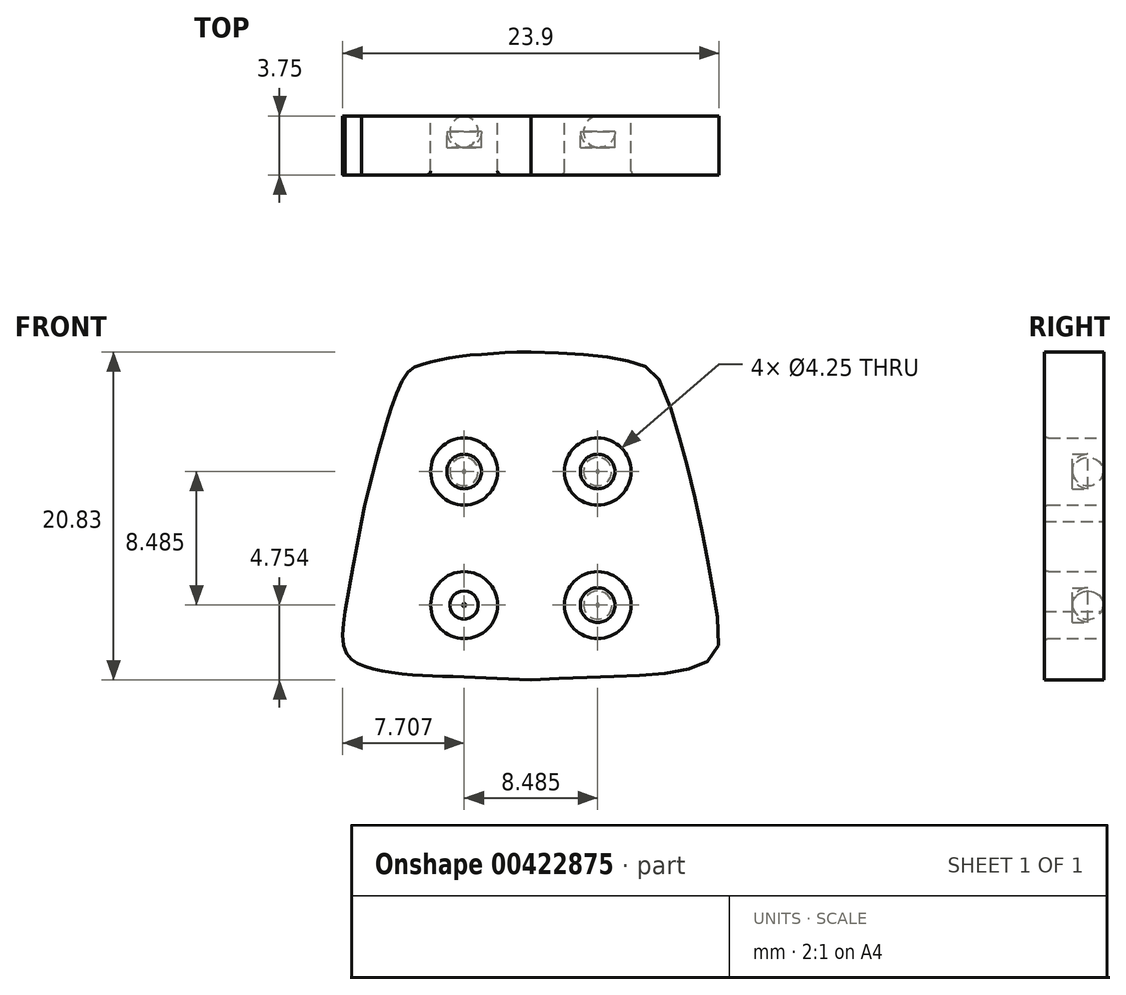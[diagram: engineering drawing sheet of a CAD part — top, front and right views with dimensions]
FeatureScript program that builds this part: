
annotation { "Feature Type Name" : "Feature", "Feature Type Description" : "" }
export const myFeature = defineFeature(function(context is Context, id is Id, definition is map)
    precondition{}
    {
        {
            var Q0;
            Q0=qCreatedBy(makeId("Front.planeOp"),FACE);
            var sketch = newSketch(context, id + "F0", { "sketchPlane" : qUnion([Q0])});
            skCircle(sketch, "E0", {"center": v(4.24, -5.22) * mm, "radius": 1.1 * mm});
            skCircle(sketch, "E1", {"center": v(-4.24, -5.22) * mm, "radius": 1.1 * mm});
            skCircle(sketch, "E2", {"center": v(-4.24, 3.27) * mm, "radius": 1.1 * mm});
            skCircle(sketch, "E3", {"center": v(4.24, 3.27) * mm, "radius": 1.1 * mm});
            skLineSegment(sketch, "E4", {"start": v(-11.8, -5.6) * mm, "end": v(-10.76, 0.08) * mm});
            skFitSpline(sketch, "E5", {"points": [v(0, 10.86) * mm, v(-2.43, 10.76) * mm, v(-4.46, 10.6) * mm, v(-6, 10.33) * mm, v(-7.12, 10) * mm, v(-7.97, 9.38) * mm, v(-9.15, 6.4) * mm, v(-9.87, 3.87) * mm, v(-10.76, 0.08) * mm, v(-11.29, -2.76) * mm, v(-11.8, -5.6) * mm, v(-11.8, -8.12) * mm, v(-10.95, -8.93) * mm, v(-9.5, -9.39) * mm, v(-7.34, -9.66) * mm, v(-5.18, -9.75) * mm, v(-2.65, -9.84) * mm, v(0, -9.97) * mm], "startDerivative": vector(-46.58, 0.42) * mm, "endDerivative": vector(41.02, -2.27) * mm});
            skFitSpline(sketch, "E6.MirrorCS", {"points": [v(0, 10.86) * mm, v(2.43, 10.76) * mm, v(4.46, 10.6) * mm, v(6, 10.33) * mm, v(7.12, 10) * mm, v(7.97, 9.38) * mm, v(9.15, 6.4) * mm, v(9.87, 3.87) * mm, v(10.76, 0.08) * mm, v(11.29, -2.76) * mm, v(11.8, -5.6) * mm, v(11.8, -8.12) * mm, v(10.95, -8.93) * mm, v(9.5, -9.39) * mm, v(7.34, -9.66) * mm, v(5.18, -9.75) * mm, v(2.65, -9.84) * mm, v(0, -9.97) * mm], "startDerivative": vector(46.58, 0.42) * mm, "endDerivative": vector(-41.02, -2.27) * mm});
            skCircle(sketch, "E7", {"center": v(4.24, 3.27) * mm, "radius": 2.12 * mm});
            skCircle(sketch, "E8", {"center": v(4.24, -5.22) * mm, "radius": 2.12 * mm});
            skCircle(sketch, "E9", {"center": v(-4.24, -5.22) * mm, "radius": 2.12 * mm});
            skCircle(sketch, "E10", {"center": v(-4.24, 3.27) * mm, "radius": 2.12 * mm});
            skSolve(sketch);
        }
        {
            var Q0;
            Q0=makeQuery(id+"F0.imprint","IMPRINT",FACE,{"disambiguationData":[TD([[makeQuery(id+"F0.imprint","IMPRINT",EDGE,{"derivedFrom":sQuery(id+"F0.wireOp",EDGE,"E0")}),1.0]])]});
            var Q1;
            {var subQ5=sQuery(id+"F0.wireOp",EDGE,"E6.MirrorCS");Q1=makeQuery(id+"F0.imprint","IMPRINT",FACE,{"disambiguationData":[TD([[makeQuery(id+"F0.imprint","IMPRINT",EDGE,{"derivedFrom":subQ5}),-1.0]])]});}
            var Q2;
            Q2=makeQuery(id+"F0.imprint","IMPRINT",FACE,{"disambiguationData":[TD([[makeQuery(id+"F0.imprint","IMPRINT",EDGE,{"derivedFrom":sQuery(id+"F0.wireOp",EDGE,"E2")}),1.0]])]});
            var Q3;
            Q3=makeQuery(id+"F0.imprint","IMPRINT",FACE,{"disambiguationData":[TD([[makeQuery(id+"F0.imprint","IMPRINT",EDGE,{"derivedFrom":sQuery(id+"F0.wireOp",EDGE,"E1")}),1.0]])]});
            var Q4;
            Q4=makeQuery(id+"F0.imprint","IMPRINT",FACE,{"disambiguationData":[TD([[makeQuery(id+"F0.imprint","IMPRINT",EDGE,{"derivedFrom":sQuery(id+"F0.wireOp",EDGE,"E3")}),1.0]])]});
            extrude(context, id + "F1", {"entities" : qUnion([Q0, Q1, Q2, Q3, Q4]), "depth" : 2 * mm});
        }
        {
            var Q0;
            {var subQ5=sQuery(id+"F0.wireOp",EDGE,"E6.MirrorCS");Q0=makeQuery(id+"F0.imprint","IMPRINT",FACE,{"disambiguationData":[TD([[makeQuery(id+"F0.imprint","IMPRINT",EDGE,{"derivedFrom":subQ5}),-1.0]])]});}
            extrude(context, id + "F2", {"entities" : qUnion([Q0]), "operationType" : NewBodyOperationType.ADD, "depth" : 3.75 * mm});
        }
        {
            var Q0;
            Q0=makeQuery(id+"F2.opExtrude","CAP_EDGE",EDGE,{"disambiguationData":[OSD([sQuery(id+"F0.wireOp",EDGE,"E10")])],"isStart":false});
            var Q1;
            Q1=makeQuery(id+"F2.opExtrude","CAP_EDGE",EDGE,{"disambiguationData":[OSD([sQuery(id+"F0.wireOp",EDGE,"E7")])],"isStart":false});
            var Q2;
            Q2=makeQuery(id+"F2.opExtrude","CAP_EDGE",EDGE,{"disambiguationData":[OSD([sQuery(id+"F0.wireOp",EDGE,"E8")])],"isStart":false});
            var Q3;
            Q3=makeQuery(id+"F2.opExtrude","CAP_EDGE",EDGE,{"disambiguationData":[OSD([sQuery(id+"F0.wireOp",EDGE,"E9")])],"isStart":false});
            fillet(context, id + "F3", {"entities" : qUnion([Q0, Q1, Q2, Q3]), "radius" : .25 * mm, "tangentPropagation" : true, "allowEdgeOverflow" : false});
        }
        {
            var Q0;
            {var subQ0=sQuery(id+"F0.wireOp",EDGE,"E5");Q0=makeQuery(id+"F2.opExtrude","CAP_EDGE",EDGE,{"disambiguationData":[OSD([subQ0]),TDD([makeQuery(id+"F0.imprint","IMPRINT",EDGE,{"disambiguationData":[TD([[makeQuery(id+"F0.imprint","INTERSECT",VERTEX,{"disambiguationData":[OD(1.0)],"derivedFrom":[sQuery(id+"F0.wireOp",EDGE,"E4"),subQ0]}),1.0]])],"derivedFrom":subQ0})])],"isStart":false});}
            var Q1;
            {var subQ0=sQuery(id+"F0.wireOp",EDGE,"E5");var subQ1=sQuery(id+"F0.wireOp",EDGE,"E4");Q1=makeQuery(id+"F2.opExtrude","CAP_EDGE",EDGE,{"disambiguationData":[OSD([subQ1]),TDD([makeQuery(id+"F0.imprint","IMPRINT",EDGE,{"disambiguationData":[TD([[makeQuery(id+"F0.imprint","INTERSECT",VERTEX,{"disambiguationData":[OD(1.0)],"derivedFrom":[subQ1,subQ0]}),1.0]])],"derivedFrom":subQ1})])],"isStart":false});}
            var Q2;
            {var subQ0=sQuery(id+"F0.wireOp",EDGE,"E9");Q2=makeQuery(id+"F3.opFillet","BLEND_EDGE",EDGE,{"blendedFrom":[makeQuery(id+"F2.opExtrude","CAP_EDGE",EDGE,{"disambiguationData":[OSD([subQ0])],"isStart":false}),makeQuery(id+"F2.opExtrude","CAP_FACE",FACE,{"disambiguationData":[OSD([sQuery(id+"F0.wireOp",EDGE,"E4"),sQuery(id+"F0.wireOp",EDGE,"E5"),sQuery(id+"F0.wireOp",EDGE,"E6.MirrorCS"),sQuery(id+"F0.wireOp",EDGE,"E7"),sQuery(id+"F0.wireOp",EDGE,"E8"),subQ0,sQuery(id+"F0.wireOp",EDGE,"E10")])],"isStart":false})],"blendedInto":[makeQuery(id+"F2.opExtrude","CAP_FACE",FACE,{"disambiguationData":[OSD([sQuery(id+"F0.wireOp",EDGE,"E4"),sQuery(id+"F0.wireOp",EDGE,"E5"),sQuery(id+"F0.wireOp",EDGE,"E6.MirrorCS"),sQuery(id+"F0.wireOp",EDGE,"E7"),sQuery(id+"F0.wireOp",EDGE,"E8"),subQ0,sQuery(id+"F0.wireOp",EDGE,"E10")])],"isStart":false})]});}
            var Q3;
            Q3=makeQuery(id+"F1.opExtrude","CAP_EDGE",EDGE,{"disambiguationData":[OSD([sQuery(id+"F0.wireOp",EDGE,"E1")])],"isStart":false});
            var Q4;
            Q4=makeQuery(id+"F1.opExtrude","CAP_EDGE",EDGE,{"disambiguationData":[OSD([sQuery(id+"F0.wireOp",EDGE,"E2")])],"isStart":true});
            var Q5;
            Q5=makeQuery(id+"F1.opExtrude","CAP_EDGE",EDGE,{"disambiguationData":[OSD([sQuery(id+"F0.wireOp",EDGE,"E3")])],"isStart":true});
            var Q6;
            Q6=makeQuery(id+"F1.opExtrude","CAP_EDGE",EDGE,{"disambiguationData":[OSD([sQuery(id+"F0.wireOp",EDGE,"E0")])],"isStart":true});
            var Q7;
            Q7=makeQuery(id+"F1.opExtrude","CAP_EDGE",EDGE,{"disambiguationData":[OSD([sQuery(id+"F0.wireOp",EDGE,"E1")])],"isStart":true});
            var Q8;
            {var subQ0=sQuery(id+"F0.wireOp",EDGE,"E7");Q8=makeQuery(id+"F3.opFillet","BLEND_EDGE",EDGE,{"blendedFrom":[makeQuery(id+"F2.opExtrude","CAP_EDGE",EDGE,{"disambiguationData":[OSD([subQ0])],"isStart":false}),makeQuery(id+"F2.opExtrude","CAP_FACE",FACE,{"disambiguationData":[OSD([sQuery(id+"F0.wireOp",EDGE,"E4"),sQuery(id+"F0.wireOp",EDGE,"E5"),sQuery(id+"F0.wireOp",EDGE,"E6.MirrorCS"),subQ0,sQuery(id+"F0.wireOp",EDGE,"E8"),sQuery(id+"F0.wireOp",EDGE,"E9"),sQuery(id+"F0.wireOp",EDGE,"E10")])],"isStart":false})],"blendedInto":[makeQuery(id+"F2.opExtrude","CAP_FACE",FACE,{"disambiguationData":[OSD([sQuery(id+"F0.wireOp",EDGE,"E4"),sQuery(id+"F0.wireOp",EDGE,"E5"),sQuery(id+"F0.wireOp",EDGE,"E6.MirrorCS"),subQ0,sQuery(id+"F0.wireOp",EDGE,"E8"),sQuery(id+"F0.wireOp",EDGE,"E9"),sQuery(id+"F0.wireOp",EDGE,"E10")])],"isStart":false})]});}
            fillet(context, id + "F4", {"entities" : qUnion([Q0, Q1, Q2, Q3, Q4, Q5, Q6, Q7, Q8]), "radius" : 1 * mm, "tangentPropagation" : true, "allowEdgeOverflow" : false});
        }
    });
